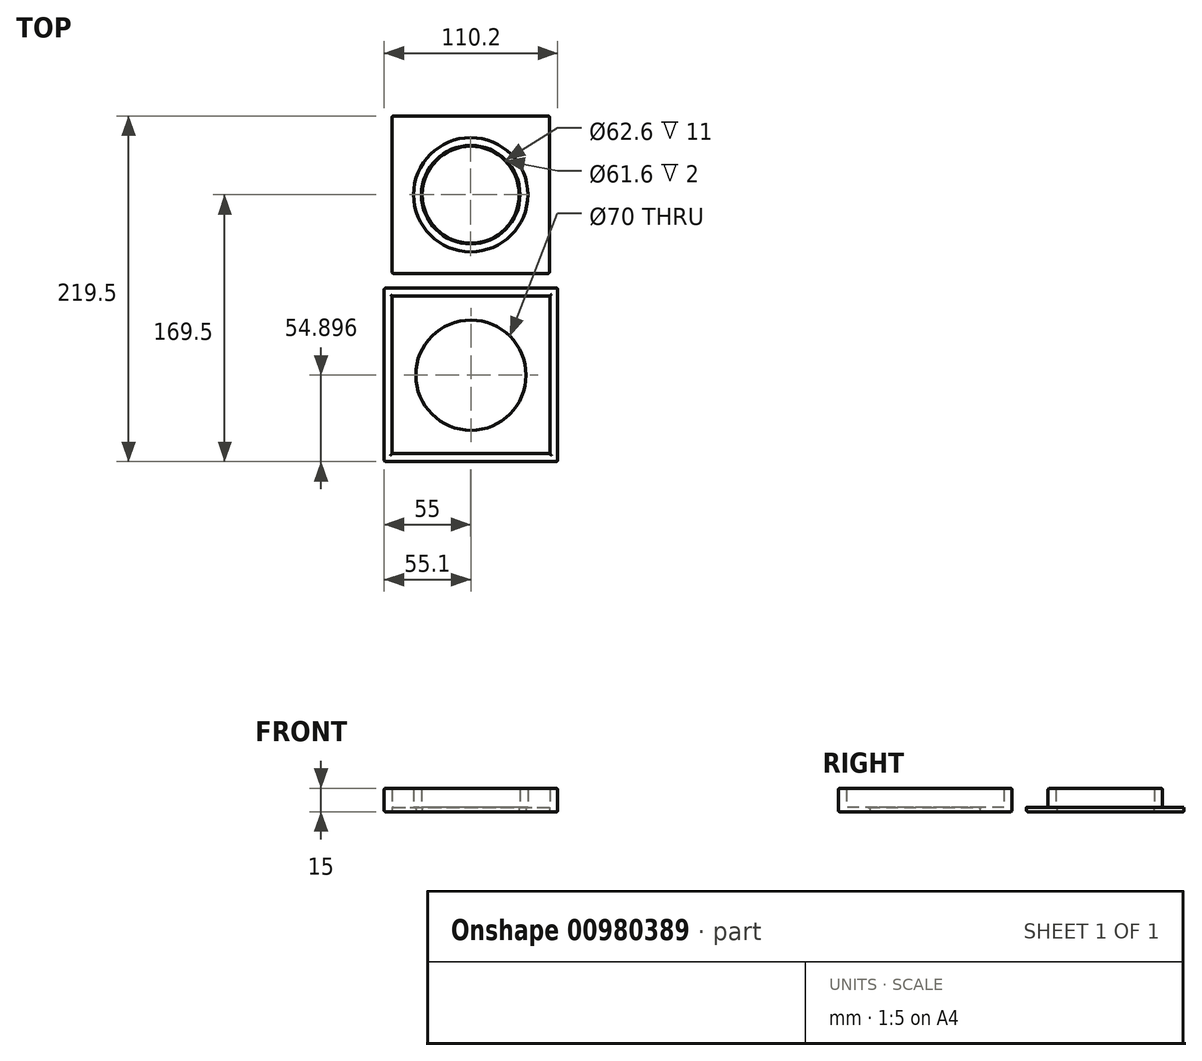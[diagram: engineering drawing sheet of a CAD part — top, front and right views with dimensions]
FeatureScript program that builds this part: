
annotation { "Feature Type Name" : "Feature", "Feature Type Description" : "" }
export const myFeature = defineFeature(function(context is Context, id is Id, definition is map)
    precondition{}
    {
        {
            var Q0;
            Q0=qCreatedBy(makeId("Top.planeOp"),FACE);
            var sketch = newSketch(context, id + "F0", { "sketchPlane" : qUnion([Q0])});
            skLineSegment(sketch, "E0.bottom", {"start": v(0, 0) * mm, "end": v(100, 0) * mm});
            skLineSegment(sketch, "E0.top", {"start": v(0, 100) * mm, "end": v(100, 100) * mm});
            skLineSegment(sketch, "E0.left", {"start": v(0, 0) * mm, "end": v(0, 100) * mm});
            skLineSegment(sketch, "E0.right", {"start": v(100, 0) * mm, "end": v(100, 100) * mm});
            skCircle(sketch, "E1", {"center": v(50, 50) * mm, "radius": 31.3 * mm});
            skPoint(sketch, "E1.centerSnap0", {"position": v(50, 100) * mm});
            skPoint(sketch, "E1.centerSnap1", {"position": v(0, 50) * mm});
            skCircle(sketch, "E2", {"center": v(50, 50) * mm, "radius": 30.8 * mm});
            skCircle(sketch, "E3", {"center": v(50, 50) * mm, "radius": 36.3 * mm});
            skCircle(sketch, "E4", {"center": v(50.1, -64.6) * mm, "radius": 35 * mm});
            skPoint(sketch, "E4.centerSnap1", {"position": v(50.1, -14.3) * mm});
            skLineSegment(sketch, "E5.0", {"start": v(-5, -9.3) * mm, "end": v(105.2, -9.3) * mm});
            skLineSegment(sketch, "E5.1", {"start": v(-5, -9.3) * mm, "end": v(-5, -119.5) * mm});
            skLineSegment(sketch, "E5.2", {"start": v(-5, -119.5) * mm, "end": v(105.2, -119.5) * mm});
            skLineSegment(sketch, "E5.3", {"start": v(105.2, -9.3) * mm, "end": v(105.2, -119.5) * mm});
            skLineSegment(sketch, "E6", {"start": v(0, -114.5) * mm, "end": v(100.2, -114.5) * mm});
            skLineSegment(sketch, "E7", {"start": v(100.2, -14.3) * mm, "end": v(100.2, -114.5) * mm});
            skLineSegment(sketch, "E8", {"start": v(0, -14.3) * mm, "end": v(0, -114.5) * mm});
            skLineSegment(sketch, "E9", {"start": v(0, -14.3) * mm, "end": v(100.2, -14.3) * mm});
            skSolve(sketch);
        }
        {
            var Q0;
            Q0=makeQuery(id+"F0.imprint","IMPRINT",FACE,{"disambiguationData":[TD([[makeQuery(id+"F0.imprint","IMPRINT",EDGE,{"derivedFrom":sQuery(id+"F0.wireOp",EDGE,"E1")}),-1.0]])]});
            var Q1;
            Q1=makeQuery(id+"F0.imprint","IMPRINT",FACE,{"disambiguationData":[TD([[makeQuery(id+"F0.imprint","IMPRINT",EDGE,{"derivedFrom":sQuery(id+"F0.wireOp",EDGE,"JDFHyrcC-VGeh-v9XD-pVOG-qxKent8c7stP.bottom")}),1.0]])]});
            var Q2;
            Q2=makeQuery(id+"F0.imprint","IMPRINT",FACE,{"disambiguationData":[TD([[makeQuery(id+"F0.imprint","IMPRINT",EDGE,{"derivedFrom":sQuery(id+"F0.wireOp",EDGE,"E5.0")}),-1.0]])]});
            extrude(context, id + "F1", {"entities" : qUnion([Q0, Q1, Q2]), "depth" : 15 * mm, "offsetDistance" : 25 * mm});
        }
        {
            var Q0;
            Q0=makeQuery(id+"F0.imprint","IMPRINT",FACE,{"disambiguationData":[TD([[makeQuery(id+"F0.imprint","IMPRINT",EDGE,{"derivedFrom":sQuery(id+"F0.wireOp",EDGE,"E1")}),1.0]])]});
            var Q1;
            Q1=makeQuery(id+"F0.imprint","IMPRINT",FACE,{"disambiguationData":[TD([[makeQuery(id+"F0.imprint","IMPRINT",EDGE,{"derivedFrom":sQuery(id+"F0.wireOp",EDGE,"E0.bottom")}),1.0]])]});
            var Q2;
            Q2=makeQuery(id+"F0.imprint","IMPRINT",FACE,{"disambiguationData":[TD([[makeQuery(id+"F0.imprint","IMPRINT",EDGE,{"derivedFrom":sQuery(id+"F0.wireOp",EDGE,"JDFHyrcC-VGeh-v9XD-pVOG-qxKent8c7stP.bottom")}),-1.0]])]});
            var Q3;
            Q3=makeQuery(id+"F0.imprint","IMPRINT",FACE,{"disambiguationData":[TD([[makeQuery(id+"F0.imprint","IMPRINT",EDGE,{"derivedFrom":sQuery(id+"F0.wireOp",EDGE,"E4")}),-1.0]])]});
            extrude(context, id + "F2", {"entities" : qUnion([Q0, Q1, Q2, Q3]), "operationType" : NewBodyOperationType.ADD, "depth" : 3 * mm, "offsetDistance" : 25 * mm});
        }
        {
            var Q0;
            Q0=makeQuery(id+"F1.opExtrude","CAP_EDGE",EDGE,{"disambiguationData":[OSD([sQuery(id+"F0.wireOp",EDGE,"E1")])],"isStart":false});
            var Q1;
            Q1=makeQuery(id+"F1.opExtrude","CAP_EDGE",EDGE,{"disambiguationData":[OSD([sQuery(id+"F0.wireOp",EDGE,"E3")])],"isStart":false});
            var Q2;
            Q2=makeQuery(id+"F2.opExtrude","CAP_EDGE",EDGE,{"disambiguationData":[OSD([sQuery(id+"F0.wireOp",EDGE,"E0.bottom")])],"isStart":true});
            var Q3;
            Q3=makeQuery(id+"F2.opExtrude","CAP_EDGE",EDGE,{"disambiguationData":[OSD([sQuery(id+"F0.wireOp",EDGE,"E0.right")])],"isStart":true});
            var Q4;
            Q4=makeQuery(id+"F2.opExtrude","CAP_EDGE",EDGE,{"disambiguationData":[OSD([sQuery(id+"F0.wireOp",EDGE,"E0.top")])],"isStart":true});
            var Q5;
            Q5=makeQuery(id+"F2.opExtrude","CAP_EDGE",EDGE,{"disambiguationData":[OSD([sQuery(id+"F0.wireOp",EDGE,"E0.left")])],"isStart":true});
            var Q6;
            Q6=makeQuery(id+"F2.opExtrude","CAP_EDGE",EDGE,{"disambiguationData":[OSD([sQuery(id+"F0.wireOp",EDGE,"E2")])],"isStart":true});
            var Q7;
            Q7=makeQuery(id+"F1.opExtrude","CAP_EDGE",EDGE,{"disambiguationData":[OSD([sQuery(id+"F0.wireOp",EDGE,"E5.3")])],"isStart":false});
            var Q8;
            Q8=makeQuery(id+"F1.opExtrude","CAP_EDGE",EDGE,{"disambiguationData":[OSD([sQuery(id+"F0.wireOp",EDGE,"E5.0")])],"isStart":false});
            var Q9;
            Q9=makeQuery(id+"F1.opExtrude","CAP_EDGE",EDGE,{"disambiguationData":[OSD([sQuery(id+"F0.wireOp",EDGE,"E5.1")])],"isStart":false});
            var Q10;
            Q10=makeQuery(id+"F1.opExtrude","CAP_EDGE",EDGE,{"disambiguationData":[OSD([sQuery(id+"F0.wireOp",EDGE,"E5.2")])],"isStart":false});
            var Q11;
            Q11=makeQuery(id+"F1.opExtrude","SWEPT_EDGE",EDGE,{"disambiguationData":[OSD([sQuery(id+"F0.wireOp",EDGE,"E5.1"),sQuery(id+"F0.wireOp",EDGE,"E5.2")])]});
            var Q12;
            Q12=makeQuery(id+"F1.opExtrude","SWEPT_EDGE",EDGE,{"disambiguationData":[OSD([sQuery(id+"F0.wireOp",EDGE,"E5.2"),sQuery(id+"F0.wireOp",EDGE,"E5.3")])]});
            var Q13;
            Q13=makeQuery(id+"F1.opExtrude","SWEPT_EDGE",EDGE,{"disambiguationData":[OSD([sQuery(id+"F0.wireOp",EDGE,"E5.0"),sQuery(id+"F0.wireOp",EDGE,"E5.3")])]});
            var Q14;
            Q14=makeQuery(id+"F1.opExtrude","SWEPT_EDGE",EDGE,{"disambiguationData":[OSD([sQuery(id+"F0.wireOp",EDGE,"E5.0"),sQuery(id+"F0.wireOp",EDGE,"E5.1")])]});
            var Q15;
            Q15=makeQuery(id+"F1.opExtrude","CAP_EDGE",EDGE,{"disambiguationData":[OSD([sQuery(id+"F0.wireOp",EDGE,"E5.0")])],"isStart":true});
            var Q16;
            Q16=makeQuery(id+"F1.opExtrude","CAP_EDGE",EDGE,{"disambiguationData":[OSD([sQuery(id+"F0.wireOp",EDGE,"E5.3")])],"isStart":true});
            var Q17;
            Q17=makeQuery(id+"F2.opExtrude","CAP_EDGE",EDGE,{"disambiguationData":[OSD([sQuery(id+"F0.wireOp",EDGE,"E4")])],"isStart":true});
            var Q18;
            Q18=makeQuery(id+"F1.opExtrude","CAP_EDGE",EDGE,{"disambiguationData":[OSD([sQuery(id+"F0.wireOp",EDGE,"E5.1")])],"isStart":true});
            var Q19;
            Q19=makeQuery(id+"F1.opExtrude","CAP_EDGE",EDGE,{"disambiguationData":[OSD([sQuery(id+"F0.wireOp",EDGE,"E5.2")])],"isStart":true});
            var Q20;
            Q20=makeQuery(id+"F2.opExtrude","CAP_EDGE",EDGE,{"disambiguationData":[OSD([sQuery(id+"F0.wireOp",EDGE,"E4")])],"isStart":false});
            var Q21;
            Q21=makeQuery(id+"F2.opExtrude","SWEPT_EDGE",EDGE,{"disambiguationData":[OSD([sQuery(id+"F0.wireOp",EDGE,"E0.top"),sQuery(id+"F0.wireOp",EDGE,"E0.right")])]});
            var Q22;
            Q22=makeQuery(id+"F2.opExtrude","SWEPT_EDGE",EDGE,{"disambiguationData":[OSD([sQuery(id+"F0.wireOp",EDGE,"E0.top"),sQuery(id+"F0.wireOp",EDGE,"E0.left")])]});
            var Q23;
            Q23=makeQuery(id+"F2.opExtrude","SWEPT_EDGE",EDGE,{"disambiguationData":[OSD([sQuery(id+"F0.wireOp",EDGE,"E0.bottom"),sQuery(id+"F0.wireOp",EDGE,"E0.left")])]});
            var Q24;
            Q24=makeQuery(id+"F2.opExtrude","SWEPT_EDGE",EDGE,{"disambiguationData":[OSD([sQuery(id+"F0.wireOp",EDGE,"E0.bottom"),sQuery(id+"F0.wireOp",EDGE,"E0.right")])]});
            var Q25;
            Q25=makeQuery(id+"F1.opExtrude","CAP_EDGE",EDGE,{"disambiguationData":[OSD([sQuery(id+"F0.wireOp",EDGE,"E8")])],"isStart":false});
            var Q26;
            Q26=makeQuery(id+"F1.opExtrude","CAP_EDGE",EDGE,{"disambiguationData":[OSD([sQuery(id+"F0.wireOp",EDGE,"E9")])],"isStart":false});
            var Q27;
            Q27=makeQuery(id+"F1.opExtrude","CAP_EDGE",EDGE,{"disambiguationData":[OSD([sQuery(id+"F0.wireOp",EDGE,"E7")])],"isStart":false});
            var Q28;
            Q28=makeQuery(id+"F1.opExtrude","CAP_EDGE",EDGE,{"disambiguationData":[OSD([sQuery(id+"F0.wireOp",EDGE,"E6")])],"isStart":false});
            fillet(context, id + "F3", {"entities" : qUnion([Q0, Q1, Q2, Q3, Q4, Q5, Q6, Q7, Q8, Q9, Q10, Q11, Q12, Q13, Q14, Q15, Q16, Q17, Q18, Q19, Q20, Q21, Q22, Q23, Q24, Q25, Q26, Q27, Q28]), "radius" : 1 * mm, "tangentPropagation" : true, "allowEdgeOverflow" : false});
        }
    });
